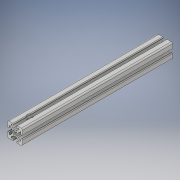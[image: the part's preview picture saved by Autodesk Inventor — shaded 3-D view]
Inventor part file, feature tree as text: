
AUTODESK INVENTOR PART (.ipt)
format: ipt  version: 2018 (Build 220112000, 112)  size: 350,208 bytes
history: native  units: in
note: dims shown in document units (in); Inventor stores cm internally (conversion verified against a paired STEP export)
features: move_body x2, direct_edit x1, extrude x1, sketch x1, projected_geometry x1, other x1
ambient origin geometry x8: Origin, YZ Plane, XZ Plane, XY Plane, X Axis, Y Axis, Z Axis, Center Point
bodies: Solid1 (feature_tree)
feature tree (7):
  direct_edit  "Direct Edit1"
  extrude  "Extrusion1"  Depth=1.5in
  sketch  "Sketch1"  dims[d0=0.0in d1=0.0in d2=14.0in d3=1.5in d4=0.5312in d5=1.0in d6=0.0in d7=0.0in d8=0.0in d9=15.0in]
  projected_geometry  "Projected Loop1"
  other  "8020-1515-S-1515-S X 145_1_1:1"
  move_body  "Move1"
  move_body  "Move2"
